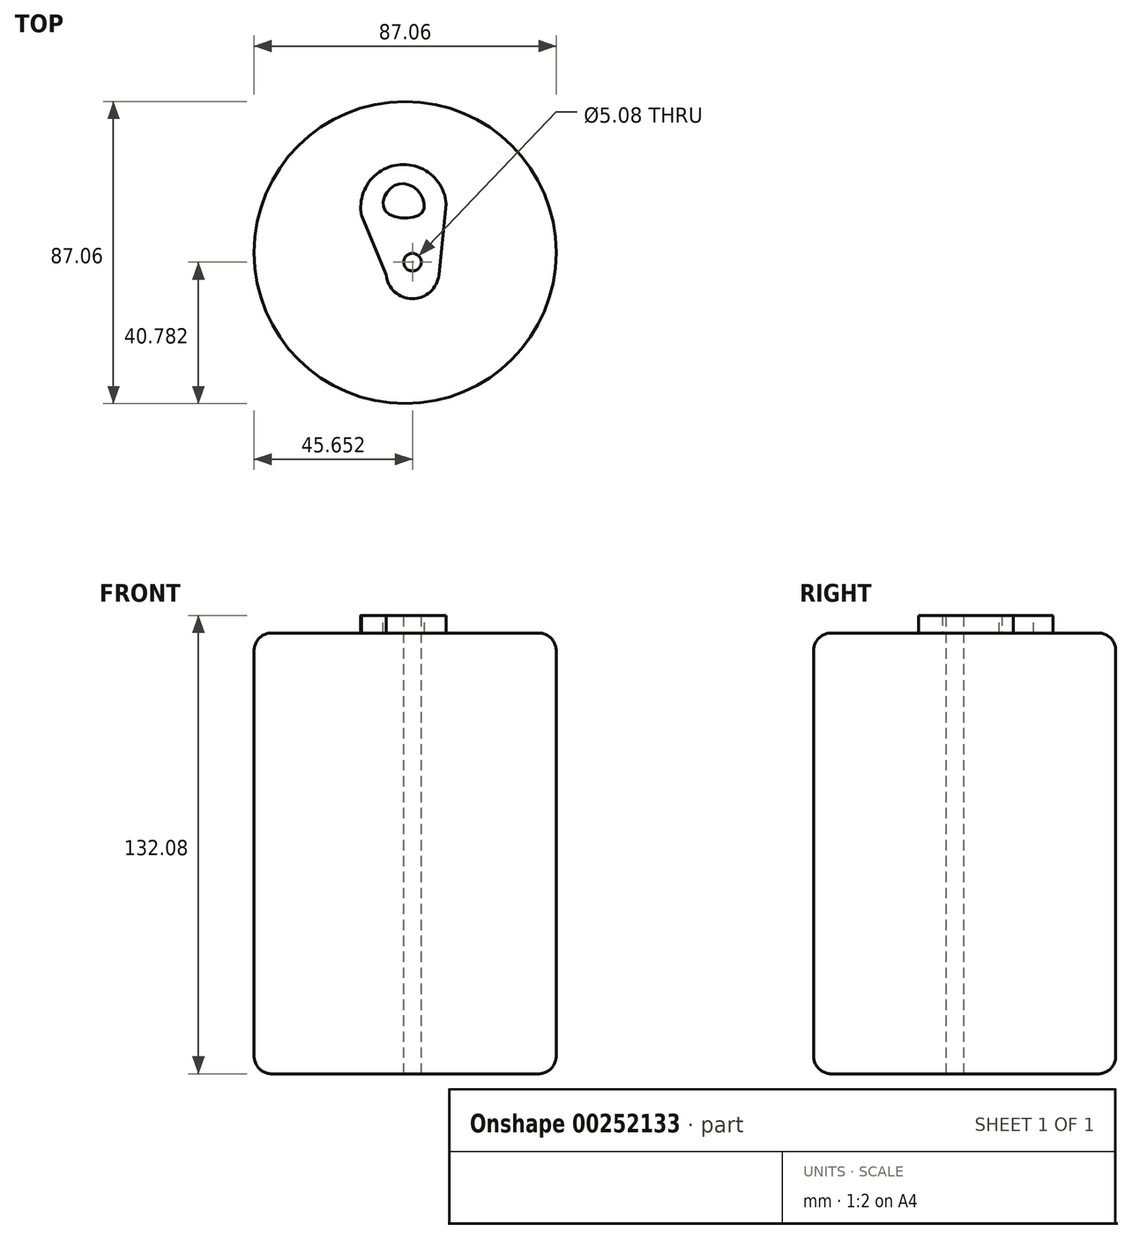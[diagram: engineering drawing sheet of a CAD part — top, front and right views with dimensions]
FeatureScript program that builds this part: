
annotation { "Feature Type Name" : "Feature", "Feature Type Description" : "" }
export const myFeature = defineFeature(function(context is Context, id is Id, definition is map)
    precondition{}
    {
        {
            var Q0;
            Q0=qCreatedBy(makeId("Top.planeOp"),FACE);
            var sketch = newSketch(context, id + "F0", { "sketchPlane" : qUnion([Q0])});
            skCircle(sketch, "E0", {"center": v(0, 0) * mm, "radius": 43.53 * mm});
            skSolve(sketch);
        }
        {
            var Q0;
            Q0=makeQuery(id+"F0.imprint","IMPRINT",FACE,{"disambiguationData":[TD([[makeQuery(id+"F0.imprint","IMPRINT",EDGE,{"derivedFrom":sQuery(id+"F0.wireOp",EDGE,"E0")}),1.0]])]});
            extrude(context, id + "F1", {"entities" : qUnion([Q0]), "depth" : 127 * mm});
        }
        {
            var Q0;
            Q0=makeQuery(id+"F1.opExtrude","SWEPT_FACE",FACE,{"disambiguationData":[OSD([sQuery(id+"F0.wireOp",EDGE,"E0")])]});
            fillet(context, id + "F2", {"entities" : qUnion([Q0]), "radius" : 5.08 * mm, "tangentPropagation" : true, "allowEdgeOverflow" : false});
        }
        {
            var Q0;
            Q0=makeQuery(id+"F1.opExtrude","CAP_FACE",FACE,{"disambiguationData":[OSD([sQuery(id+"F0.wireOp",EDGE,"E0")])],"isStart":false});
            var sketch = newSketch(context, id + "F3", { "sketchPlane" : qUnion([Q0])});
            skArc(sketch, "E1", {"start": v(11.85, 14.06) * mm, "mid": v(-2.13, 25.26) * mm, "end": v(-12.55, 10.7) * mm});
            skLineSegment(sketch, "E2", {"start": v(-12.55, 10.7) * mm, "end": v(-5.48, -6.45) * mm});
            skLineSegment(sketch, "E3", {"start": v(11.85, 14.06) * mm, "end": v(9.72, -6.45) * mm});
            skArc(sketch, "E4", {"start": v(-5.48, -6.45) * mm, "mid": v(2.12, -13.3) * mm, "end": v(9.72, -6.45) * mm});
            skSolve(sketch);
        }
        {
            var Q0;
            Q0=makeQuery(id+"F3.imprint","IMPRINT",FACE,{"disambiguationData":[TD([[makeQuery(id+"F3.imprint","IMPRINT",EDGE,{"derivedFrom":sQuery(id+"F3.wireOp",EDGE,"E1")}),1.0]])]});
            extrude(context, id + "F4", {"entities" : qUnion([Q0]), "operationType" : NewBodyOperationType.ADD, "depth" : 5.08 * mm});
        }
        {
            var Q0;
            Q0=makeQuery(id+"F4.opExtrude","CAP_FACE",FACE,{"disambiguationData":[OSD([sQuery(id+"F3.wireOp",EDGE,"E1"),sQuery(id+"F3.wireOp",EDGE,"E2"),sQuery(id+"F3.wireOp",EDGE,"E3"),sQuery(id+"F3.wireOp",EDGE,"E4")])],"isStart":false});
            var sketch = newSketch(context, id + "F5", { "sketchPlane" : qUnion([Q0])});
            skFitSpline(sketch, "E5", {"points": [v(-5.66, 12) * mm, v(-3.54, 19) * mm, v(3.54, 18) * mm, v(4.6, 11.25) * mm, v(-5.66, 12) * mm]});
            skSolve(sketch);
        }
        {
            var Q0;
            Q0=makeQuery(id+"F5.imprint","IMPRINT",FACE,{"disambiguationData":[TD([[makeQuery(id+"F5.imprint","IMPRINT",EDGE,{"derivedFrom":sQuery(id+"F5.wireOp",EDGE,"E5")}),-1.0]])]});
            extrude(context, id + "F6", {"entities" : qUnion([Q0]), "operationType" : NewBodyOperationType.REMOVE, "oppositeDirection" : true, "depth" : 5.08 * mm});
        }
        {
            var Q0;
            Q0=makeQuery(id+"F4.opExtrude","CAP_FACE",FACE,{"disambiguationData":[OSD([sQuery(id+"F3.wireOp",EDGE,"E1"),sQuery(id+"F3.wireOp",EDGE,"E2"),sQuery(id+"F3.wireOp",EDGE,"E3"),sQuery(id+"F3.wireOp",EDGE,"E4")])],"isStart":false});
            var sketch = newSketch(context, id + "F7", { "sketchPlane" : qUnion([Q0])});
            skLineSegment(sketch, "E6", {"start": v(2.12, -2.75) * mm, "end": v(2.12, 2.75) * mm});
            skSolve(sketch);
        }
        {
            var Q0;
            Q0=sQuery(id+"F7.wireOp",VERTEX,"E6.start");
            var Q1;
            Q1=makeQuery(id+"F1.opExtrude","SWEPT_BODY",BODY,{"disambiguationData":[OSD([sQuery(id+"F0.wireOp",EDGE,"E0")])]});
            hole(context, id + "F8", {"style" : HoleStyle.SIMPLE, "endStyle" : HoleEndStyle.THROUGH, "holeDiameter" : 5.08 * mm, "tappedDepth" : 12.7 * mm, "tapClearance" : 3, "locations" : qUnion([Q0]), "scope" : qUnion([Q1])});
        }
    });
